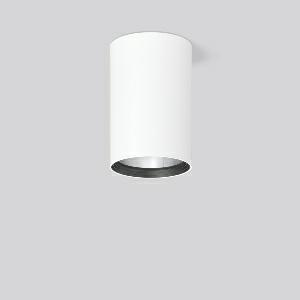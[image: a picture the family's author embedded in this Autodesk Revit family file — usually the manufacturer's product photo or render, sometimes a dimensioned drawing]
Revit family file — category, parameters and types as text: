
# Revit family: heledon_maxi_a_931217_002_2_76_25f9
name_source: partatom
category: Lighting Fixtures
units: mm (PartAtom-declared; Revit-internal decimal feet)

## family parameters
Cut with Voids When Loaded = No
Host = Face
Light Source = No
Part Type = Normal
Room Calculation Point = No
Round Connector Dimension = Use Diameter
Shared = No

## types (1)
- HELEDON maxi A (1 x LED Modul 927, 3150 lm, 2700)
    Apparent Load = 25 VA
    Approval mark = CE
    CIE Flux Codes = 100 100 100 100 100
    Color Rendering = 92
    Color Temperature = 2700
    Default Elevation = 1800 mm
    Description = Series: HELEDON maxi
Cylindrical surface-mounted downlight. Housing: die-cast aluminium, powder-coated. Internal ceiling frame polycarbonate with bayonet mounting. Black plastic ring and recessed LED to prevent glare from the side. Optical assembly with reflector made of MIRO-Silver with 98% total light reflection for outstanding efficiency - can be changed without tools. Best colour rendering index Ra>90. Suitable for Ceiling mounting. Easy installation with a separate ceiling frame with bayonet mounting and plug connection. Driver integrated. Connected via plug-in connector. High quality converter without flickering and stroboscopic effect. The following accessories can be mounted without use of tools: interchangeable lenses, decorative glasses, honeycomb louvre, clear and frosted diffusers, white interchangeable plastic ring. 
Colour: traffic white, matt (RAL 9016)
Diameter: 123 mm
Height: 183 mm
Lamp: LED
Socket: without socket
Colour temperature: 2700K
Colour rendering index (CRI): 92
System power: 25 W
Rated luminous flux: 3150 lm
Luminous efficiency: 126 lm/W
Control gear: Converter, dimmable, DALI
Protection class: I
Type of protection: IP 20
    Height = 183 mm
    Lamp = 1 x LED Modul 927
    Lamp Light Flux = 3150 lm
    Lamp count = 1
    Length = 123 mm
    Lifetime = 50000 h
    Luminous efficacy = 126 lm/W
    Manufacturer = RZB
    ModVariant = No
    Model = 931217.002.2.76
    Mounting Place = Ceiling
    Mounting Type = Surface mounted
    Number of Poles = 1
    OnlyDefault = Yes
    Power Factor = 1
    Product Name = HELEDON maxi A
    Product group = Surface mounted downlights
    ProductGroupID = 302
    Protection Class = Protection class I
    Protection Degree = IP 20
    RLX_Detail_Level = 1
    RLX_Emergency_Light_Flux = 0 lm
    RLX_Emergency_Type = 0
    RLX_Emergency_Type_DB = No
    RlxData = <blob elided: 97721 chars, md5=71876e5a>
    Socket = socket
    Standby Power = 0 W
    System Light Flux = 3150 lm
    System Power = 25 W
    Type Comments = Product without accessories
    Type Image = 931192.002.jpg
    URL = http://relux.com
    VarID = ---
    Voltage = 230 V
    Voltage Range = 220-240 V
    Weight = 0.00 kg
    Width = 0 mm  [stored 0 ft]

note: [stored X ft] marks values corroborated as IEEE doubles in the binary element streams (Revit-internal decimal feet)

## geometry (parser evidence)
native form markers: Blend x4, Sweep x9
no freeform markers — native parametric forms only
